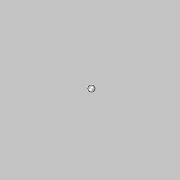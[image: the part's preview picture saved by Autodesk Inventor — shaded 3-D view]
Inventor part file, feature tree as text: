
AUTODESK INVENTOR PART (.ipt)
format: ipt  version: 2017 (Build 210142000, 142)  size: 138,752 bytes
history: native  units: mm
features: sketch x7, extrude x6, fillet x1, chamfer x1, revolve x1, projected_geometry x1
ambient origin geometry x8: Origin, YZ Plane, XZ Plane, XY Plane, X Axis, Y Axis, Z Axis, Center Point
bodies: Solid1 (feature_tree)
feature tree (17):
  extrude  "Extrusion1"  Depth=52.0mm TaperAngle=0.0deg
  fillet  "Fillet1"  Radius=8.0mm
  extrude  "Extrusion2"  Depth=4.0mm TaperAngle=0.0deg
  extrude  "Extrusion3"  Depth=82.0mm
  chamfer  "Chamfer1"  Distance=110.0mm
  extrude  "Extrusion4"  Depth=124.0mm
  extrude  "Extrusion5"  Depth=75.0mm TaperAngle=0.0deg
  revolve  "Revolution1"  [1 undecoded]
  extrude  "Extrusion6"  Depth=118.0mm
  sketch  "Sketch1"  dims[d0=80.0mm d1=52.0mm d2=0.0mm d3=8.0mm]
  sketch  "Sketch2"  dims[d4=65.0mm d5=4.0mm d6=0.0mm]
  sketch  "Sketch3"  dims[d7=48.0mm d8=82.0mm]
  sketch  "Sketch4"  dims[d9=73.0mm]
  sketch  "Sketch5"  dims[d10=91.0mm]
  projected_geometry  "Projected Loop1"
  sketch  "Sketch6"  dims[d11=5.0mm d12=110.0mm d13=0.0mm]
  sketch  "Sketch7"  dims[d14=15.0mm d15=2.0mm d16=45.0deg d17=124.0mm d18=75.0mm d19=0.0mm d20=75.0mm d21=0.0mm d22=118.0mm d23=15.0mm d24=10.0mm d25=7.0mm d27=8.0mm d28=0.872665mm d29=44.0mm d30=400.0mm d31=90.0deg d32=30.0mm d33=86.0mm d34=75.0mm d35=0.0mm d38=0.0mm]
note: 1 required parameter value undecoded (feature->parameter linkage not recoverable at this tier; creation-order binding heuristic only, values carry confidence <= 0.55)
